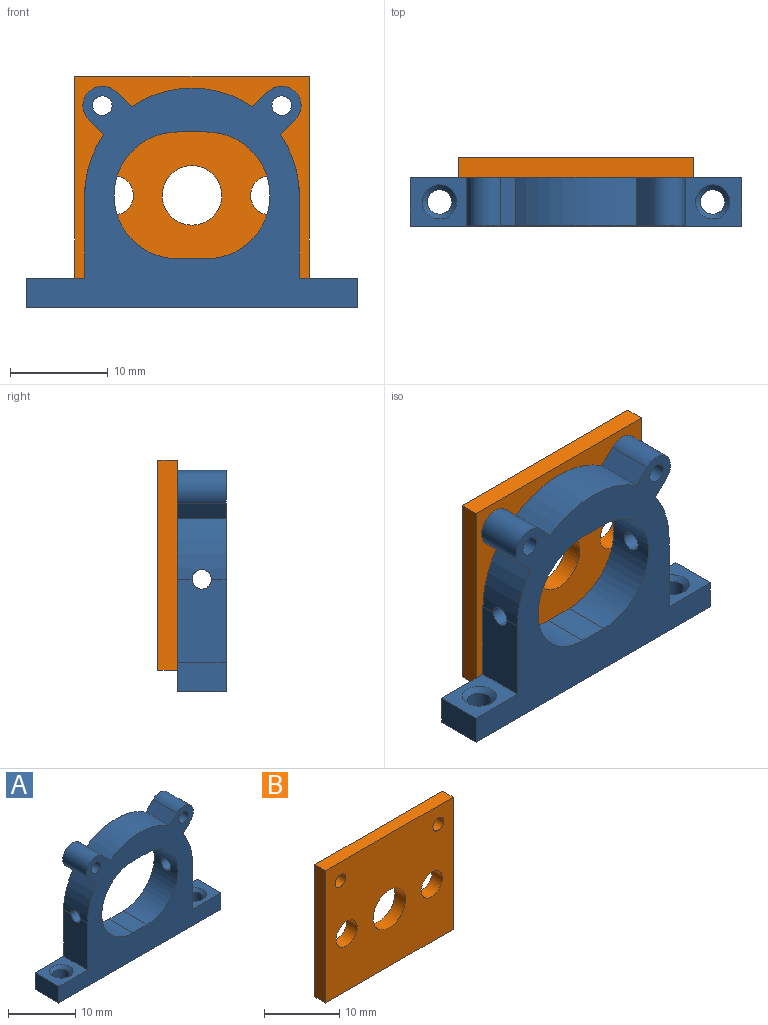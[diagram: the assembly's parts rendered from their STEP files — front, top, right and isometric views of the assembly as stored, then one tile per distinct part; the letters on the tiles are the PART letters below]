
ASSEMBLY  parts=2 mates=1
PART A: 30 faces, bbox 34x5x22.7 mm
  f0: plane 5x3mm, normal (0,0,-1), area 15mm2, adj f1,f21,f22,f23
  f1: cylinder r=6.5mm len=13mm, axis (0,1,0), area 99mm2, adj f0,f2,f22,f23,f29
  f2: plane 5x3mm, normal (0,0,1), area 15mm2, adj f1,f21,f22,f23
  f3: plane 6x5mm, normal (0,0,1), area 20.4mm2, adj f4,f20,f22,f23,f25
  f4: plane 8.5x5mm, normal (1,0,0), area 40.9mm2, adj f3,f5,f22,f23,f29
  f5: cylinder r=11mm len=6.23mm, axis (0,1,0), area 31.6mm2, adj f4,f6,f22,f23,f29
  f6: plane 5x1.54mm, normal (0.71,0,-0.71), area 10.9mm2, adj f5,f7,f22,f23
  f7: cylinder r=2mm len=5mm, axis (0,1,0), area 31.4mm2, adj f6,f8,f22,f23
  f8: plane 5x1.54mm, normal (-0.71,0,0.71), area 10.9mm2, adj f7,f9,f22,f23
  f9: cylinder r=11mm len=12.47mm, axis (0,1,0), area 66.3mm2, adj f8,f10,f22,f23
  f10: plane 5x1.54mm, normal (0.71,0,0.71), area 10.9mm2, adj f9,f11,f22,f23
  f11: cylinder r=2mm len=5mm, axis (0,1,0), area 31.4mm2, adj f10,f12,f22,f23
  f12: plane 5x1.54mm, normal (-0.71,0,-0.71), area 10.9mm2, adj f11,f13,f22,f23
  f13: cylinder r=11mm len=6.23mm, axis (0,1,0), area 31.6mm2, adj f12,f14,f22,f23,f28
  f14: plane 8.5x5mm, normal (-1,0,0), area 40.9mm2, adj f13,f15,f22,f23,f28
  f15: plane 6x5mm, normal (0,0,1), area 20.4mm2, adj f14,f16,f22,f23,f27
  f16: plane 5x3mm, normal (-1,0,0), area 15mm2, adj f15,f17,f22,f23
  f17: plane 34x5mm, normal (0,0,-1), area 160.2mm2, adj f16,f20,f22,f23,f24,f26
  f18: cylinder r=1mm len=5mm, axis (0,1,0), area 31.4mm2, adj f22,f23
  f19: cylinder r=1mm len=5mm, axis (0,1,0), area 31.4mm2, adj f22,f23
  f20: plane 5x3mm, normal (1,0,0), area 15mm2, adj f3,f17,f22,f23
  f21: cylinder r=6.5mm len=13mm, axis (0,1,0), area 98.9mm2, adj f0,f2,f22,f23,f28
  f22: plane 34x22.69mm, normal (0,-1,0), area 330.1mm2, adj f0,f1,f2,f3,f4,f5,f6,f7
  f23: plane 34x22.69mm, normal (0,1,0), area 330.1mm2, adj f0,f1,f2,f3,f4,f5,f6,f7
  f24: cylinder r=1.25mm len=2.5mm, axis (0,0,1), area 19.6mm2, adj f17,f25
  f25: cone r=1.25mm half-angle=45deg, axis (0,0,1), area 6.7mm2, adj f3,f24
  f26: cylinder r=1.25mm len=2.5mm, axis (0,0,1), area 19.6mm2, adj f17,f27
  f27: cone r=1.25mm half-angle=45deg, axis (0,0,1), area 6.7mm2, adj f15,f26
  f28: cylinder r=1mm len=3.08mm, axis (1,0,0), area 19mm2, adj f13,f14,f21
  f29: cylinder r=1mm len=3.08mm, axis (1,0,0), area 19mm2, adj f1,f4,f5
PART B: 11 faces, bbox 24x2x21.5 mm
  f0: plane 24x2mm, normal (0,0,1), area 48mm2, adj f1,f7,f9,f10
  f1: plane 21.5x2mm, normal (-1,0,0), area 43mm2, adj f0,f2,f9,f10
  f2: plane 24x2mm, normal (0,0,-1), area 48mm2, adj f1,f7,f9,f10
  f3: cylinder r=1mm len=2mm, axis (0,1,0), area 12.6mm2, adj f9,f10
  f4: cylinder r=3.05mm len=6.1mm, axis (0,1,0), area 38.3mm2, adj f9,f10
  f5: cylinder r=1mm len=2mm, axis (0,1,0), area 12.6mm2, adj f9,f10
  f6: cylinder r=2mm len=4mm, axis (0,1,0), area 25.1mm2, adj f9,f10
  f7: plane 21.5x2mm, normal (1,0,0), area 43mm2, adj f0,f2,f9,f10
  f8: cylinder r=2mm len=4mm, axis (0,1,0), area 25.1mm2, adj f9,f10
  f9: plane 24x21.5mm, normal (0,-1,0), area 455.4mm2, adj f0,f1,f2,f3,f4,f5,f6,f7
  f10: plane 24x21.5mm, normal (0,1,0), area 455.4mm2, adj f0,f1,f2,f3,f4,f5,f6,f7
PLACE A t=(-1.47,-7.35,-2.06)mm
PLACE B t=(-1.47,-5.35,-2.06)mm
MATE fastened B.f3 <-> A.f11  axis (0,-1,0) through (-10.67,-7.35,7.13)mm
